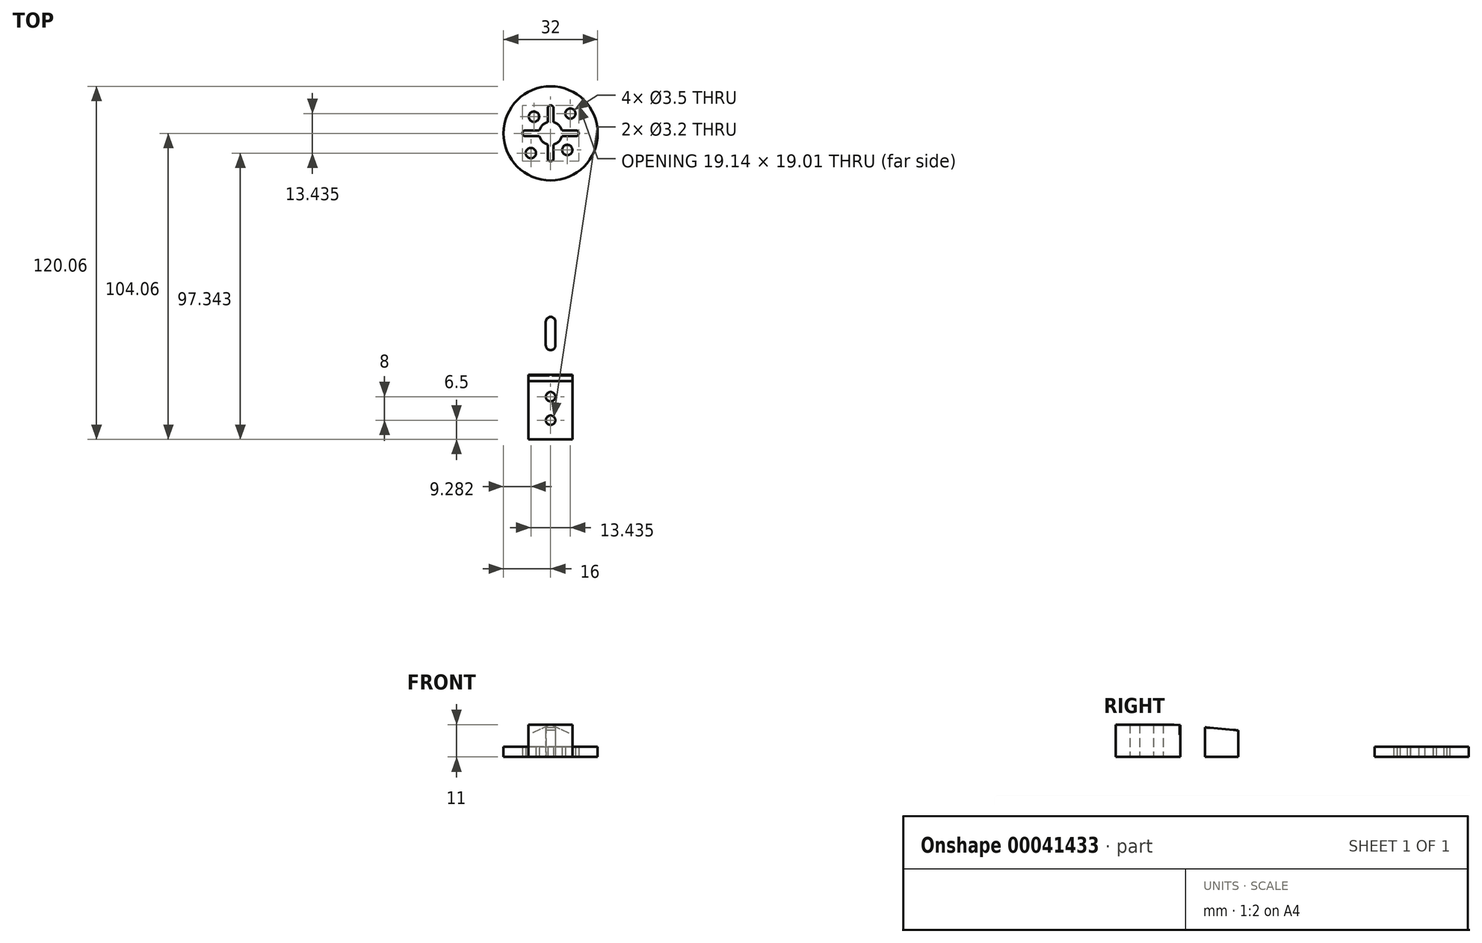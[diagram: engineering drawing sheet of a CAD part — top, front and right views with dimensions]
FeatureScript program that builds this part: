
annotation { "Feature Type Name" : "Feature", "Feature Type Description" : "" }
export const myFeature = defineFeature(function(context is Context, id is Id, definition is map)
    precondition{}
    {
        {
            var Q0;
            Q0=qCreatedBy(makeId("Top.planeOp"),FACE);
            var sketch = newSketch(context, id + "F0", { "sketchPlane" : qUnion([Q0])});
            skCircle(sketch, "E0", {"center": v(0, 0) * mm, "radius": 16 * mm});
            skArc(sketch, "E1", {"start": v(-3.82, -1) * mm, "mid": v(-2.8, -2.8) * mm, "end": v(-1, -3.82) * mm});
            skLineSegment(sketch, "E2", {"start": v(-23.4, 0) * mm, "end": v(23.53, 0) * mm, "construction": true});
            skLineSegment(sketch, "E3", {"start": v(0, 20.34) * mm, "end": v(0, -20.32) * mm, "construction": true});
            skLineSegment(sketch, "E4.0", {"start": v(-8.68, -1) * mm, "end": v(-3.82, -1) * mm});
            skCircle(sketch, "E5", {"center": v(0, 0) * mm, "radius": 8.5 * mm, "construction": true});
            skArc(sketch, "E6", {"start": v(1, 8.44) * mm, "mid": v(0, 9.5) * mm, "end": v(-1, 8.44) * mm});
            skArc(sketch, "E7.MirrorCS", {"start": v(1, -8.44) * mm, "mid": v(0, -9.5) * mm, "end": v(-1, -8.44) * mm});
            skArc(sketch, "E8", {"start": v(-8.44, 1) * mm, "mid": v(-9.57, 0) * mm, "end": v(-8.44, -1) * mm});
            skArc(sketch, "E9.MirrorCS", {"start": v(8.44, 1) * mm, "mid": v(9.57, 0) * mm, "end": v(8.44, -1) * mm});
            skLineSegment(sketch, "E10.trimOffspring", {"start": v(-8.68, 1) * mm, "end": v(-3.82, 1) * mm});
            skLineSegment(sketch, "E11.trimOffspring", {"start": v(1, 8.57) * mm, "end": v(1, 3.82) * mm});
            skLineSegment(sketch, "E12.trimOffspring", {"start": v(-1, 8.57) * mm, "end": v(-1, 3.82) * mm});
            skArc(sketch, "E13.trimOffspring", {"start": v(1, -3.82) * mm, "mid": v(2.8, -2.8) * mm, "end": v(3.82, -1) * mm});
            skArc(sketch, "E14.trimOffspring", {"start": v(3.82, 1) * mm, "mid": v(2.8, 2.8) * mm, "end": v(1, 3.82) * mm});
            skArc(sketch, "E15.trimOffspring", {"start": v(-1, 3.82) * mm, "mid": v(-2.8, 2.8) * mm, "end": v(-3.82, 1) * mm});
            skLineSegment(sketch, "E16.trimOffspring", {"start": v(3.82, 1) * mm, "end": v(8.68, 1) * mm});
            skLineSegment(sketch, "E17.trimOffspring", {"start": v(3.82, -1) * mm, "end": v(8.68, -1) * mm});
            skLineSegment(sketch, "E18.trimOffspring", {"start": v(1, -3.82) * mm, "end": v(1, -8.57) * mm});
            skLineSegment(sketch, "E19.trimOffspring", {"start": v(-1, -3.82) * mm, "end": v(-1, -8.57) * mm});
            skLineSegment(sketch, "E20", {"start": v(11.31, -11.31) * mm, "end": v(-11.31, 11.31) * mm, "construction": true});
            skLineSegment(sketch, "E21", {"start": v(11.31, 11.31) * mm, "end": v(-11.31, -11.31) * mm, "construction": true});
            skCircle(sketch, "E22", {"center": v(0, 0) * mm, "radius": 8 * mm, "construction": true});
            skCircle(sketch, "E23", {"center": v(5.66, -5.66) * mm, "radius": 1.75 * mm});
            skCircle(sketch, "E24.MirrorC", {"center": v(-5.66, 5.66) * mm, "radius": 1.75 * mm});
            skCircle(sketch, "E25", {"center": v(0, 0) * mm, "radius": 9.5 * mm, "construction": true});
            skCircle(sketch, "E26", {"center": v(6.72, 6.72) * mm, "radius": 1.75 * mm});
            skCircle(sketch, "E27.MirrorC", {"center": v(-6.72, -6.72) * mm, "radius": 1.75 * mm});
            skSolve(sketch);
        }
        {
            var Q0;
            Q0=makeQuery(id+"F0.imprint","IMPRINT",FACE,{"disambiguationData":[TD([[makeQuery(id+"F0.imprint","IMPRINT",EDGE,{"derivedFrom":sQuery(id+"F0.wireOp",EDGE,"E0")}),1.0]])]});
            extrude(context, id + "F1", {"entities" : qUnion([Q0]), "depth" : 3.5 * mm});
        }
        {
            var Q0;
            Q0=qCreatedBy(makeId("Top.planeOp"),FACE);
            var sketch = newSketch(context, id + "F2", { "sketchPlane" : qUnion([Q0])});
            skLineSegment(sketch, "E28", {"start": v(-27.39, 15.94) * mm, "end": v(26.63, 15.94) * mm, "construction": true});
            skPoint(sketch, "E29.orphan", {"position": v(0, 15.94) * mm});
            skLineSegment(sketch, "E30.0", {"start": v(-7.5, -104.06) * mm, "end": v(7.5, -104.06) * mm});
            skLineSegment(sketch, "E31", {"start": v(0, -20.37) * mm, "end": v(0, -104.06) * mm, "construction": true});
            skLineSegment(sketch, "E32.0", {"start": v(-7.5, -82.06) * mm, "end": v(-7.5, -104.06) * mm});
            skLineSegment(sketch, "E33.MirrorCS", {"start": v(7.5, -82.06) * mm, "end": v(7.5, -104.06) * mm});
            skLineSegment(sketch, "E34.0", {"start": v(-7.5, -82.06) * mm, "end": v(7.5, -82.06) * mm});
            skPoint(sketch, "E35.orphan", {"position": v(-7.5, -20.37) * mm});
            skPoint(sketch, "E36.orphan", {"position": v(7.5, -20.37) * mm});
            skLineSegment(sketch, "E37.0", {"start": v(-7.5, -97.56) * mm, "end": v(7.5, -97.56) * mm, "construction": true});
            skLineSegment(sketch, "E38.0", {"start": v(-7.5, -89.56) * mm, "end": v(7.5, -89.56) * mm, "construction": true});
            skCircle(sketch, "E39", {"center": v(0, -89.56) * mm, "radius": 1.6 * mm});
            skCircle(sketch, "E40", {"center": v(0, -97.56) * mm, "radius": 1.6 * mm});
            skSolve(sketch);
        }
        {
            var Q0;
            Q0=makeQuery(id+"F2.imprint","IMPRINT",FACE,{"disambiguationData":[TD([[makeQuery(id+"F2.imprint","IMPRINT",EDGE,{"derivedFrom":sQuery(id+"F2.wireOp",EDGE,"E30.0")}),1.0]])]});
            extrude(context, id + "F3", {"entities" : qUnion([Q0]), "depth" : 11 * mm});
        }
        {
            var Q0;
            Q0=qCreatedBy(makeId("Top.planeOp"),FACE);
            var sketch = newSketch(context, id + "F4", { "sketchPlane" : qUnion([Q0])});
            skLineSegment(sketch, "E41", {"start": v(0, 0) * mm, "end": v(0, -82.08) * mm, "construction": true});
            skLineSegment(sketch, "E42.0", {"start": v(-7.5, 0) * mm, "end": v(-7.5, -82.08) * mm, "construction": true});
            skLineSegment(sketch, "E43.0", {"start": v(7.5, 0) * mm, "end": v(7.5, -82.08) * mm, "construction": true});
            skLineSegment(sketch, "E44", {"start": v(0, 0) * mm, "end": v(-16, 0) * mm, "construction": true});
            skLineSegment(sketch, "E45", {"start": v(-16, 0) * mm, "end": v(-7.5, -82.08) * mm});
            skLineSegment(sketch, "E46", {"start": v(-16, 0) * mm, "end": v(0, 0) * mm});
            skLineSegment(sketch, "E47.MirrorCS", {"start": v(16, 0) * mm, "end": v(7.5, -82.08) * mm});
            skLineSegment(sketch, "E48.MirrorCS", {"start": v(16, 0) * mm, "end": v(0, 0) * mm});
            skArc(sketch, "E49", {"start": v(-16, 0) * mm, "mid": v(0, -16) * mm, "end": v(16, 0) * mm});
            skLineSegment(sketch, "E50", {"start": v(7.5, -82.08) * mm, "end": v(-7.5, -82.08) * mm});
            skSolve(sketch);
        }
        {
            var Q0;
            {var subQ5=sQuery(id+"F4.wireOp",EDGE,"E50");Q0=makeQuery(id+"F4.imprint","IMPRINT",FACE,{"disambiguationData":[TD([[makeQuery(id+"F4.imprint","IMPRINT",EDGE,{"derivedFrom":subQ5}),-1.0]])]});}
            extrude(context, id + "F5", {"entities" : qUnion([Q0]), "depth" : 11 * mm});
        }
        {
            var Q0;
            Q0=qCreatedBy(makeId("Front.planeOp"),FACE);
            var sketch = newSketch(context, id + "F6", { "sketchPlane" : qUnion([Q0])});
            skLineSegment(sketch, "E51", {"start": v(0, 0) * mm, "end": v(-42.48, 0) * mm, "construction": true});
            skLineSegment(sketch, "E52.0", {"start": v(0, 3.5) * mm, "end": v(-42.48, 3.5) * mm, "construction": true});
            skLineSegment(sketch, "E53", {"start": v(0, 0) * mm, "end": v(0, 13.74) * mm, "construction": true});
            skLineSegment(sketch, "E54", {"start": v(0, 11.02) * mm, "end": v(-15.98, 3.5) * mm});
            skLineSegment(sketch, "E55", {"start": v(-15.98, 3.5) * mm, "end": v(-15.98, 11.02) * mm});
            skLineSegment(sketch, "E56", {"start": v(0, 11.02) * mm, "end": v(-15.98, 11.02) * mm});
            skLineSegment(sketch, "E57.MirrorCS", {"start": v(0, 11.02) * mm, "end": v(15.98, 3.5) * mm});
            skLineSegment(sketch, "E58.MirrorCS", {"start": v(0, 11.02) * mm, "end": v(15.98, 11.02) * mm});
            skLineSegment(sketch, "E59.MirrorCS", {"start": v(15.98, 3.5) * mm, "end": v(15.98, 11.02) * mm});
            skLineSegment(sketch, "E60", {"start": v(0, 3.5) * mm, "end": v(-3.44, 9.4) * mm});
            skLineSegment(sketch, "E61", {"start": v(-3.44, 9.4) * mm, "end": v(0, 11.02) * mm});
            skLineSegment(sketch, "E62.MirrorCS", {"start": v(0, 3.5) * mm, "end": v(3.44, 9.4) * mm});
            skLineSegment(sketch, "E63.MirrorCS", {"start": v(3.44, 9.4) * mm, "end": v(0, 11.02) * mm});
            skSolve(sketch);
        }
        {
            var Q0;
            Q0=makeQuery(id+"F6.imprint","IMPRINT",FACE,{"disambiguationData":[TD([[makeQuery(id+"F6.imprint","IMPRINT",EDGE,{"derivedFrom":sQuery(id+"F6.wireOp",EDGE,"E57.MirrorCS")}),1.0]])]});
            var Q1;
            Q1=makeQuery(id+"F6.imprint","IMPRINT",FACE,{"disambiguationData":[TD([[makeQuery(id+"F6.imprint","IMPRINT",EDGE,{"derivedFrom":sQuery(id+"F6.wireOp",EDGE,"E54")}),-1.0]])]});
            var Q2;
            Q2=makeQuery(id+"F3.opExtrude","SWEPT_BODY",BODY,{"disambiguationData":[OSD([sQuery(id+"F2.wireOp",EDGE,"E30.0"),sQuery(id+"F2.wireOp",EDGE,"E32.0"),sQuery(id+"F2.wireOp",EDGE,"E33.MirrorCS"),sQuery(id+"F2.wireOp",EDGE,"E34.0"),sQuery(id+"F2.wireOp",EDGE,"E39"),sQuery(id+"F2.wireOp",EDGE,"E40")])]});
            extrude(context, id + "F7", {"entities" : qUnion([Q0, Q1]), "operationType" : NewBodyOperationType.REMOVE, "endBoundEntityBody" : qUnion([Q2]), "depth" : 82.35 * mm});
        }
        {
            var Q0;
            Q0=qCreatedBy(makeId("Right.planeOp"),FACE);
            var sketch = newSketch(context, id + "F8", { "sketchPlane" : qUnion([Q0])});
            skLineSegment(sketch, "E64", {"start": v(0, 0) * mm, "end": v(0, 23.02) * mm, "construction": true});
            skLineSegment(sketch, "E65", {"start": v(-89.94, 0) * mm, "end": v(-89.94, 17.1) * mm, "construction": true});
            skLineSegment(sketch, "E66", {"start": v(0, 3.5) * mm, "end": v(-89.94, 11.5) * mm});
            skLineSegment(sketch, "E67", {"start": v(-89.94, 11.5) * mm, "end": v(0, 11.5) * mm});
            skLineSegment(sketch, "E68", {"start": v(0, 11.5) * mm, "end": v(0, 3.5) * mm});
            skSolve(sketch);
        }
        {
            var Q0;
            Q0=makeQuery(id+"F8.imprint","IMPRINT",FACE,{"disambiguationData":[TD([[makeQuery(id+"F8.imprint","IMPRINT",EDGE,{"derivedFrom":sQuery(id+"F8.wireOp",EDGE,"E66")}),-1.0]])]});
            extrude(context, id + "F9", {"entities" : qUnion([Q0]), "operationType" : NewBodyOperationType.REMOVE, "oppositeDirection" : true, "depth" : 44.1 * mm, "symmetric" : true});
        }
        {
            var Q0;
            {var subQ0=sQuery(id+"F4.wireOp",EDGE,"E50");Q0=makeQuery(id+"F4.imprint","IMPRINT",FACE,{"disambiguationData":[TD([[makeQuery(id+"F4.imprint","IMPRINT",EDGE,{"derivedFrom":subQ0}),-1.0]])]});}
            var sketch = newSketch(context, id + "F10", { "sketchPlane" : qUnion([Q0])});
            skLineSegment(sketch, "E69", {"start": v(0, -65.77) * mm, "end": v(0, -14.49) * mm, "construction": true});
            skLineSegment(sketch, "E70", {"start": v(0, -64.08) * mm, "end": v(0, -72.08) * mm, "construction": true});
            skArc(sketch, "E71.0.startCap", {"start": v(-1.65, -64.08) * mm, "mid": v(0, -62.43) * mm, "end": v(1.65, -64.08) * mm});
            skArc(sketch, "E71.0.endCap", {"start": v(1.65, -72.08) * mm, "mid": v(0, -73.73) * mm, "end": v(-1.65, -72.08) * mm});
            skLineSegment(sketch, "E71.0.left", {"start": v(1.65, -64.08) * mm, "end": v(1.65, -72.08) * mm});
            skLineSegment(sketch, "E71.0.right", {"start": v(-1.65, -64.08) * mm, "end": v(-1.65, -72.08) * mm});
            skSolve(sketch);
        }
        {
            var Q0;
            Q0=makeQuery(id+"F10.imprint","IMPRINT",FACE,{"disambiguationData":[TD([[makeQuery(id+"F10.imprint","IMPRINT",EDGE,{"derivedFrom":sQuery(id+"F10.wireOp",EDGE,"E71.0.startCap")}),-1.0]])]});
            extrude(context, id + "F11", {"entities" : qUnion([Q0]), "operationType" : NewBodyOperationType.REMOVE, "depth" : 25 * mm});
        }
        {
            var Q0;
            Q0=makeQuery(id+"F1.opExtrude","SWEPT_BODY",BODY,{"disambiguationData":[OSD([sQuery(id+"F0.wireOp",EDGE,"E0"),sQuery(id+"F0.wireOp",EDGE,"E1"),sQuery(id+"F0.wireOp",EDGE,"E4.0"),sQuery(id+"F0.wireOp",EDGE,"E6"),sQuery(id+"F0.wireOp",EDGE,"E7.MirrorCS"),sQuery(id+"F0.wireOp",EDGE,"E8"),sQuery(id+"F0.wireOp",EDGE,"E9.MirrorCS"),sQuery(id+"F0.wireOp",EDGE,"E10.trimOffspring"),sQuery(id+"F0.wireOp",EDGE,"E11.trimOffspring"),sQuery(id+"F0.wireOp",EDGE,"E12.trimOffspring"),sQuery(id+"F0.wireOp",EDGE,"E13.trimOffspring"),sQuery(id+"F0.wireOp",EDGE,"E14.trimOffspring"),sQuery(id+"F0.wireOp",EDGE,"E15.trimOffspring"),sQuery(id+"F0.wireOp",EDGE,"E16.trimOffspring"),sQuery(id+"F0.wireOp",EDGE,"E17.trimOffspring"),sQuery(id+"F0.wireOp",EDGE,"E18.trimOffspring"),sQuery(id+"F0.wireOp",EDGE,"E19.trimOffspring"),sQuery(id+"F0.wireOp",EDGE,"E23"),sQuery(id+"F0.wireOp",EDGE,"E24.MirrorC"),sQuery(id+"F0.wireOp",EDGE,"E26"),sQuery(id+"F0.wireOp",EDGE,"E27.MirrorC")])]});
            transform(context, id + "F12", {"entities" : qUnion([Q0]), "transformType" : TransformType.TRANSLATION_3D, "dx" : 0 * mm, "dy" : 0 * mm, "dz" : 0 * mm, "makeCopy" : true});
        }
        {
            var Q0;
            Q0=makeQuery(id+"F12.opPattern","COPY",BODY,{"derivedFrom":makeQuery(id+"F1.opExtrude","SWEPT_BODY",BODY,{"disambiguationData":[OSD([sQuery(id+"F0.wireOp",EDGE,"E0"),sQuery(id+"F0.wireOp",EDGE,"E1"),sQuery(id+"F0.wireOp",EDGE,"E4.0"),sQuery(id+"F0.wireOp",EDGE,"E6"),sQuery(id+"F0.wireOp",EDGE,"E7.MirrorCS"),sQuery(id+"F0.wireOp",EDGE,"E8"),sQuery(id+"F0.wireOp",EDGE,"E9.MirrorCS"),sQuery(id+"F0.wireOp",EDGE,"E10.trimOffspring"),sQuery(id+"F0.wireOp",EDGE,"E11.trimOffspring"),sQuery(id+"F0.wireOp",EDGE,"E12.trimOffspring"),sQuery(id+"F0.wireOp",EDGE,"E13.trimOffspring"),sQuery(id+"F0.wireOp",EDGE,"E14.trimOffspring"),sQuery(id+"F0.wireOp",EDGE,"E15.trimOffspring"),sQuery(id+"F0.wireOp",EDGE,"E16.trimOffspring"),sQuery(id+"F0.wireOp",EDGE,"E17.trimOffspring"),sQuery(id+"F0.wireOp",EDGE,"E18.trimOffspring"),sQuery(id+"F0.wireOp",EDGE,"E19.trimOffspring"),sQuery(id+"F0.wireOp",EDGE,"E23"),sQuery(id+"F0.wireOp",EDGE,"E24.MirrorC"),sQuery(id+"F0.wireOp",EDGE,"E26"),sQuery(id+"F0.wireOp",EDGE,"E27.MirrorC")])]}),"instanceName":"1"});
            deleteBodies(context, id + "F13", {"entities" : qUnion([Q0])});
        }
    });
